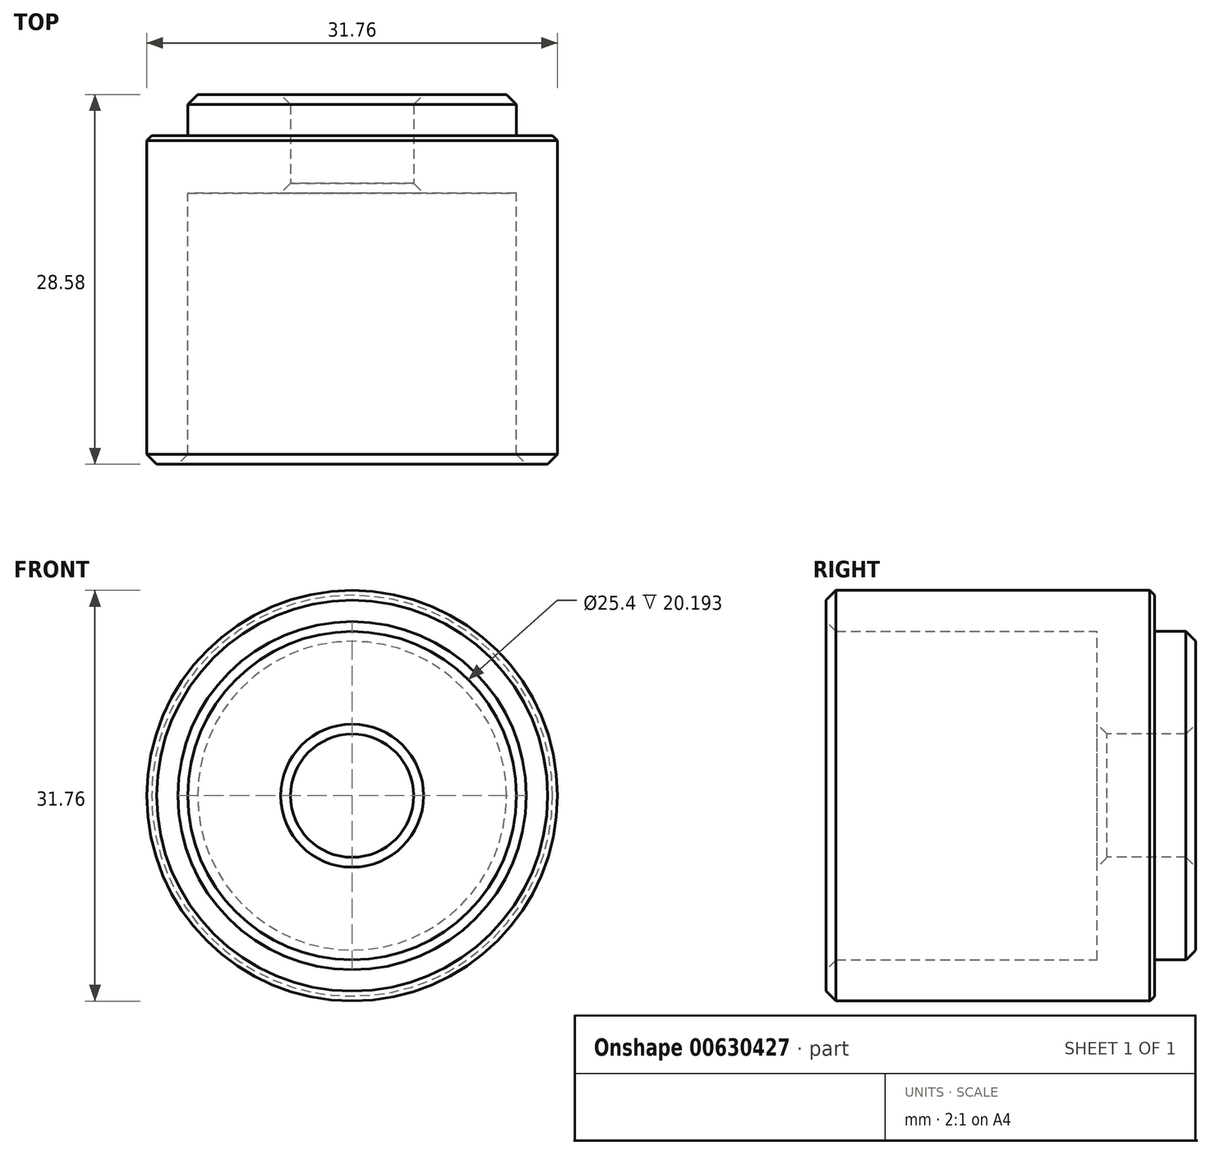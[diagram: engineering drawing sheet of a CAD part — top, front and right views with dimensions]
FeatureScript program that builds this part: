
annotation { "Feature Type Name" : "Feature", "Feature Type Description" : "" }
export const myFeature = defineFeature(function(context is Context, id is Id, definition is map)
    precondition{}
    {
        {
            var Q0;
            Q0=qCreatedBy(makeId("Front.planeOp"),FACE);
            var sketch = newSketch(context, id + "F0", { "sketchPlane" : qUnion([Q0])});
            skCircle(sketch, "E0", {"center": v(0, 0) * mm, "radius": 12.7 * mm});
            skCircle(sketch, "E1", {"center": v(0, 0) * mm, "radius": 4.76 * mm});
            skSolve(sketch);
        }
        {
            var Q0;
            Q0=makeQuery(id+"F0.imprint","IMPRINT",FACE,{"disambiguationData":[TD([[makeQuery(id+"F0.imprint","IMPRINT",EDGE,{"derivedFrom":sQuery(id+"F0.wireOp",EDGE,"E0")}),1.0]])]});
            extrude(context, id + "F1", {"entities" : qUnion([Q0]), "oppositeDirection" : true, "depth" : 3.17 * mm, "offsetDistance" : 25.4 * mm});
        }
        {
            var Q0;
            Q0=qCreatedBy(makeId("Front.planeOp"),FACE);
            var sketch = newSketch(context, id + "F2", { "sketchPlane" : qUnion([Q0])});
            skCircle(sketch, "E2", {"center": v(0, 0) * mm, "radius": 15.88 * mm});
            skCircle(sketch, "E3", {"center": v(0, 0) * mm, "radius": 4.76 * mm});
            skSolve(sketch);
        }
        {
            var Q0;
            Q0=makeQuery(id+"F2.imprint","IMPRINT",FACE,{"disambiguationData":[TD([[makeQuery(id+"F2.imprint","IMPRINT",EDGE,{"derivedFrom":sQuery(id+"F2.wireOp",EDGE,"E2")}),1.0]])]});
            extrude(context, id + "F3", {"entities" : qUnion([Q0]), "operationType" : NewBodyOperationType.ADD, "depth" : 4.44 * mm, "offsetDistance" : 25.4 * mm});
        }
        {
            var Q0;
            Q0=qCreatedBy(makeId("Front.planeOp"),FACE);
            var sketch = newSketch(context, id + "F4", { "sketchPlane" : qUnion([Q0])});
            skCircle(sketch, "E4", {"center": v(0, 0) * mm, "radius": 15.88 * mm});
            skCircle(sketch, "E5", {"center": v(0, 0) * mm, "radius": 12.7 * mm});
            skSolve(sketch);
        }
        {
            var Q0;
            Q0=makeQuery(id+"F4.imprint","IMPRINT",FACE,{"disambiguationData":[TD([[makeQuery(id+"F4.imprint","IMPRINT",EDGE,{"derivedFrom":sQuery(id+"F4.wireOp",EDGE,"E4")}),1.0]])]});
            extrude(context, id + "F5", {"entities" : qUnion([Q0]), "operationType" : NewBodyOperationType.ADD, "depth" : 25.4 * mm, "offsetDistance" : 25.4 * mm});
        }
        {
            var Q0;
            Q0=makeQuery(id+"F5.opExtrude","CAP_EDGE",EDGE,{"disambiguationData":[OSD([sQuery(id+"F4.wireOp",EDGE,"E5")])],"isStart":false});
            var Q1;
            Q1=makeQuery(id+"F5.opExtrude","CAP_EDGE",EDGE,{"disambiguationData":[OSD([sQuery(id+"F4.wireOp",EDGE,"E4")])],"isStart":false});
            var Q2;
            Q2=makeQuery(id+"F3.opExtrude","CAP_EDGE",EDGE,{"disambiguationData":[OSD([sQuery(id+"F2.wireOp",EDGE,"E3")])],"isStart":false});
            var Q3;
            Q3=makeQuery(id+"F1.opExtrude","CAP_EDGE",EDGE,{"disambiguationData":[OSD([sQuery(id+"F0.wireOp",EDGE,"E0")])],"isStart":false});
            var Q4;
            Q4=makeQuery(id+"F1.opExtrude","CAP_EDGE",EDGE,{"disambiguationData":[OSD([sQuery(id+"F0.wireOp",EDGE,"E1")])],"isStart":false});
            chamfer(context, id + "F6", {"entities" : qUnion([Q0, Q1, Q2, Q3, Q4]), "width" : 0.76 * mm, "tangentPropagation" : true});
        }
        {
            var Q0;
            Q0=makeQuery(id+"F3.opExtrude","CAP_EDGE",EDGE,{"disambiguationData":[OSD([sQuery(id+"F2.wireOp",EDGE,"E2")])],"isStart":true});
            chamfer(context, id + "F7", {"entities" : qUnion([Q0]), "width" : 0.38 * mm, "tangentPropagation" : true});
        }
    });
